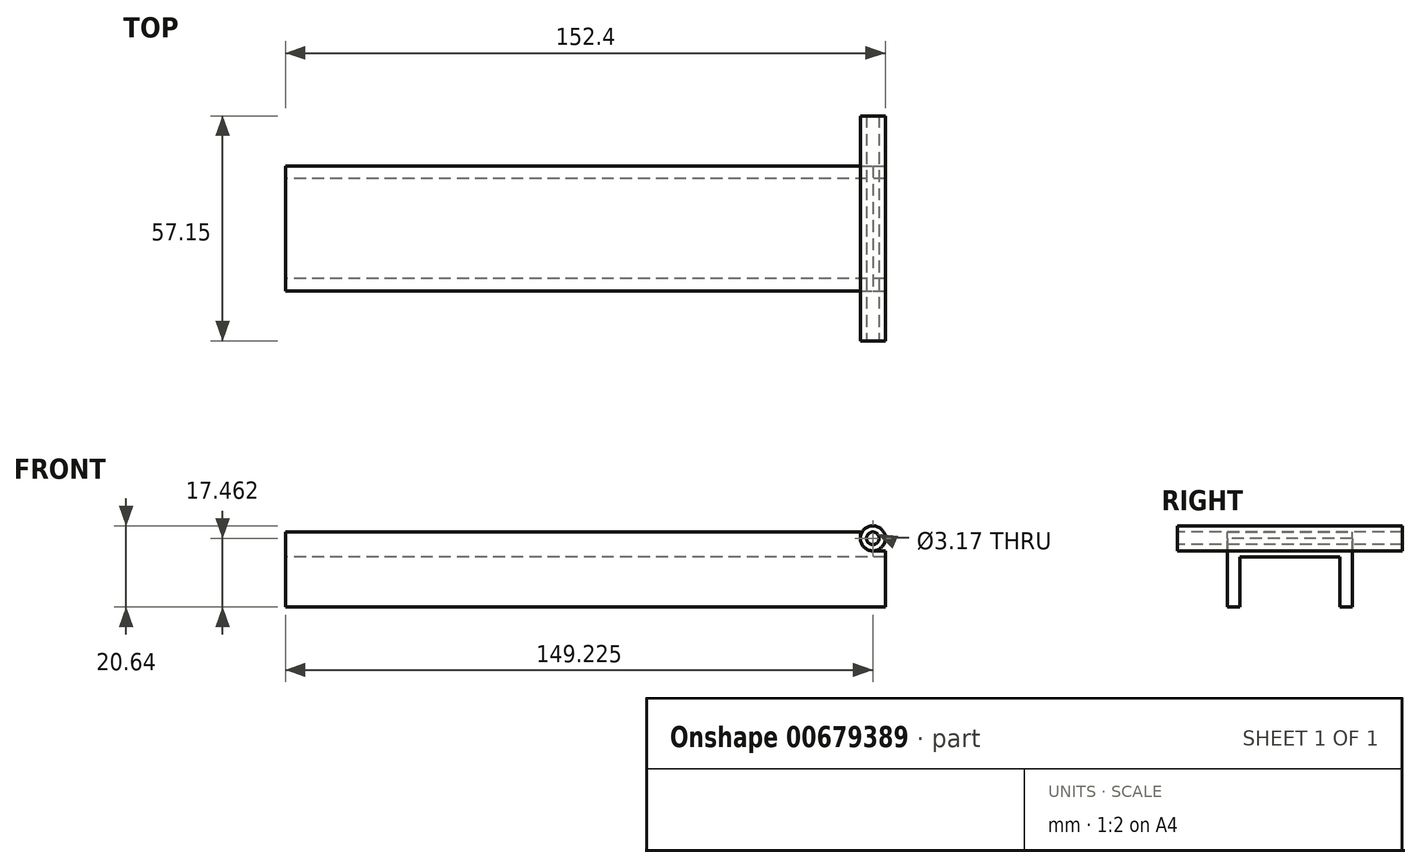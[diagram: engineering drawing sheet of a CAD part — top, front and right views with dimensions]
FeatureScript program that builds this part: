
annotation { "Feature Type Name" : "Feature", "Feature Type Description" : "" }
export const myFeature = defineFeature(function(context is Context, id is Id, definition is map)
    precondition{}
    {
        {
            var Q0;
            Q0=qCreatedBy(makeId("Right.planeOp"),FACE);
            var sketch = newSketch(context, id + "F0", { "sketchPlane" : qUnion([Q0])});
            skLineSegment(sketch, "E0.bottom", {"start": v(0, 0) * mm, "end": v(31.75, 0) * mm});
            skLineSegment(sketch, "E0.top", {"start": v(0, 15.88) * mm, "end": v(31.75, 15.88) * mm});
            skLineSegment(sketch, "E0.left", {"start": v(0, 0) * mm, "end": v(0, 15.88) * mm});
            skLineSegment(sketch, "E0.right", {"start": v(31.75, 0) * mm, "end": v(31.75, 15.88) * mm});
            skLineSegment(sketch, "E1.top", {"start": v(3.18, 12.7) * mm, "end": v(28.57, 12.7) * mm});
            skLineSegment(sketch, "E1.left", {"start": v(3.18, 0) * mm, "end": v(3.17, 12.7) * mm});
            skLineSegment(sketch, "E1.right", {"start": v(28.58, 0) * mm, "end": v(28.57, 12.7) * mm});
            skSolve(sketch);
        }
        {
            var Q0;
            Q0=makeQuery(id+"F0.imprint","IMPRINT",FACE,{"disambiguationData":[TD([[makeQuery(id+"F0.imprint","IMPRINT",EDGE,{"derivedFrom":sQuery(id+"F0.wireOp",EDGE,"E0.top")}),-1.0]])]});
            extrude(context, id + "F1", {"entities" : qUnion([Q0]), "depth" : 152.4 * mm, "offsetDistance" : 25.4 * mm});
        }
        {
            var Q0;
            Q0=makeQuery(id+"F1.opExtrude","SWEPT_FACE",FACE,{"disambiguationData":[OSD([sQuery(id+"F0.wireOp",EDGE,"E0.top")])]});
            var sketch = newSketch(context, id + "F2", { "sketchPlane" : qUnion([Q0])});
            skLineSegment(sketch, "E2.bottom", {"start": v(0, 0) * mm, "end": v(152.4, 0) * mm});
            skLineSegment(sketch, "E2.top", {"start": v(0, 31.75) * mm, "end": v(152.4, 31.75) * mm});
            skLineSegment(sketch, "E2.left", {"start": v(0, 0) * mm, "end": v(0, 31.75) * mm});
            skLineSegment(sketch, "E2.right", {"start": v(152.4, 0) * mm, "end": v(152.4, 31.75) * mm});
            skSolve(sketch);
        }
        {
            var Q0;
            Q0 = qSketchRegion(id + "F2", true);
            extrude(context, id + "F3", {"entities" : qUnion([Q0]), "operationType" : NewBodyOperationType.ADD, "depth" : 3.17 * mm, "offsetDistance" : 25.4 * mm});
        }
        {
            var Q0;
            Q0=makeQuery(id+"F3.boolean.opBoolean","MERGE",FACE,{"derivedFrom":[makeQuery(id+"F1.opExtrude","SWEPT_FACE",FACE,{"disambiguationData":[OSD([sQuery(id+"F0.wireOp",EDGE,"E0.left")])]}),makeQuery(id+"F3.opExtrude","SWEPT_FACE",FACE,{"disambiguationData":[OSD([sQuery(id+"F2.wireOp",EDGE,"E2.bottom")])]})]});
            var sketch = newSketch(context, id + "F4", { "sketchPlane" : qUnion([Q0])});
            skArc(sketch, "E3", {"start": v(146.05, 17.46) * mm, "mid": v(146.98, 15.22) * mm, "end": v(149.22, 14.29) * mm});
            skLineSegment(sketch, "E4", {"start": v(152.4, 19.05) * mm, "end": v(152.4, 17.46) * mm});
            skLineSegment(sketch, "E5", {"start": v(152.4, 19.05) * mm, "end": v(151.97, 19.05) * mm});
            skLineSegment(sketch, "E6", {"start": v(146.05, 17.46) * mm, "end": v(146.05, 19.05) * mm});
            skLineSegment(sketch, "E7", {"start": v(146.05, 19.05) * mm, "end": v(151.97, 19.05) * mm});
            skLineSegment(sketch, "E8", {"start": v(149.22, 14.29) * mm, "end": v(152.4, 14.29) * mm});
            skLineSegment(sketch, "E9", {"start": v(152.4, 14.29) * mm, "end": v(152.4, 17.46) * mm});
            skSolve(sketch);
        }
        {
            var Q0;
            Q0 = qSketchRegion(id + "F4", true);
            extrude(context, id + "F5", {"entities" : qUnion([Q0]), "operationType" : NewBodyOperationType.REMOVE, "endBound" : BoundingType.THROUGH_ALL, "oppositeDirection" : true, "depth" : 25.4 * mm, "offsetDistance" : 25.4 * mm});
        }
        {
            var Q0;
            Q0=qCreatedBy(makeId("Front.planeOp"),FACE);
            cPlane(context, id + "F6", {"entities" : qUnion([Q0]), "cplaneType" : CPlaneType.OFFSET, "offset" : 15.88 * mm, "oppositeDirection" : true, "width" : 152.4 * mm, "height" : 152.4 * mm});
        }
        {
            var Q0;
            Q0=qCreatedBy(id+"F6.planeOp",FACE);
            var sketch = newSketch(context, id + "F7", { "sketchPlane" : qUnion([Q0])});
            skCircle(sketch, "E10", {"center": v(149.23, 17.46) * mm, "radius": 3.18 * mm});
            skSolve(sketch);
        }
        {
            var Q0;
            Q0=makeQuery(id+"F7.imprint","IMPRINT",FACE,{"disambiguationData":[TD([[makeQuery(id+"F7.imprint","IMPRINT",EDGE,{"derivedFrom":sQuery(id+"F7.wireOp",EDGE,"E10")}),1.0]])]});
            extrude(context, id + "F8", {"entities" : qUnion([Q0]), "operationType" : NewBodyOperationType.ADD, "depth" : 28.57 * mm, "offsetDistance" : 25.4 * mm, "hasSecondDirection" : true, "secondDirectionOppositeDirection" : true, "secondDirectionDepth" : 28.57 * mm});
        }
        {
            var Q0;
            Q0=makeQuery(id+"F8.opExtrude","CAP_FACE",FACE,{"disambiguationData":[OSD([sQuery(id+"F7.wireOp",EDGE,"E10")])],"isStart":false});
            var sketch = newSketch(context, id + "F9", { "sketchPlane" : qUnion([Q0])});
            skCircle(sketch, "E11", {"center": v(149.23, 17.46) * mm, "radius": 1.59 * mm});
            skSolve(sketch);
        }
        {
            var Q0;
            Q0 = qSketchRegion(id + "F9", true);
            extrude(context, id + "F10", {"entities" : qUnion([Q0]), "operationType" : NewBodyOperationType.REMOVE, "endBound" : BoundingType.THROUGH_ALL, "oppositeDirection" : true, "depth" : 25.4 * mm, "offsetDistance" : 25.4 * mm});
        }
    });
